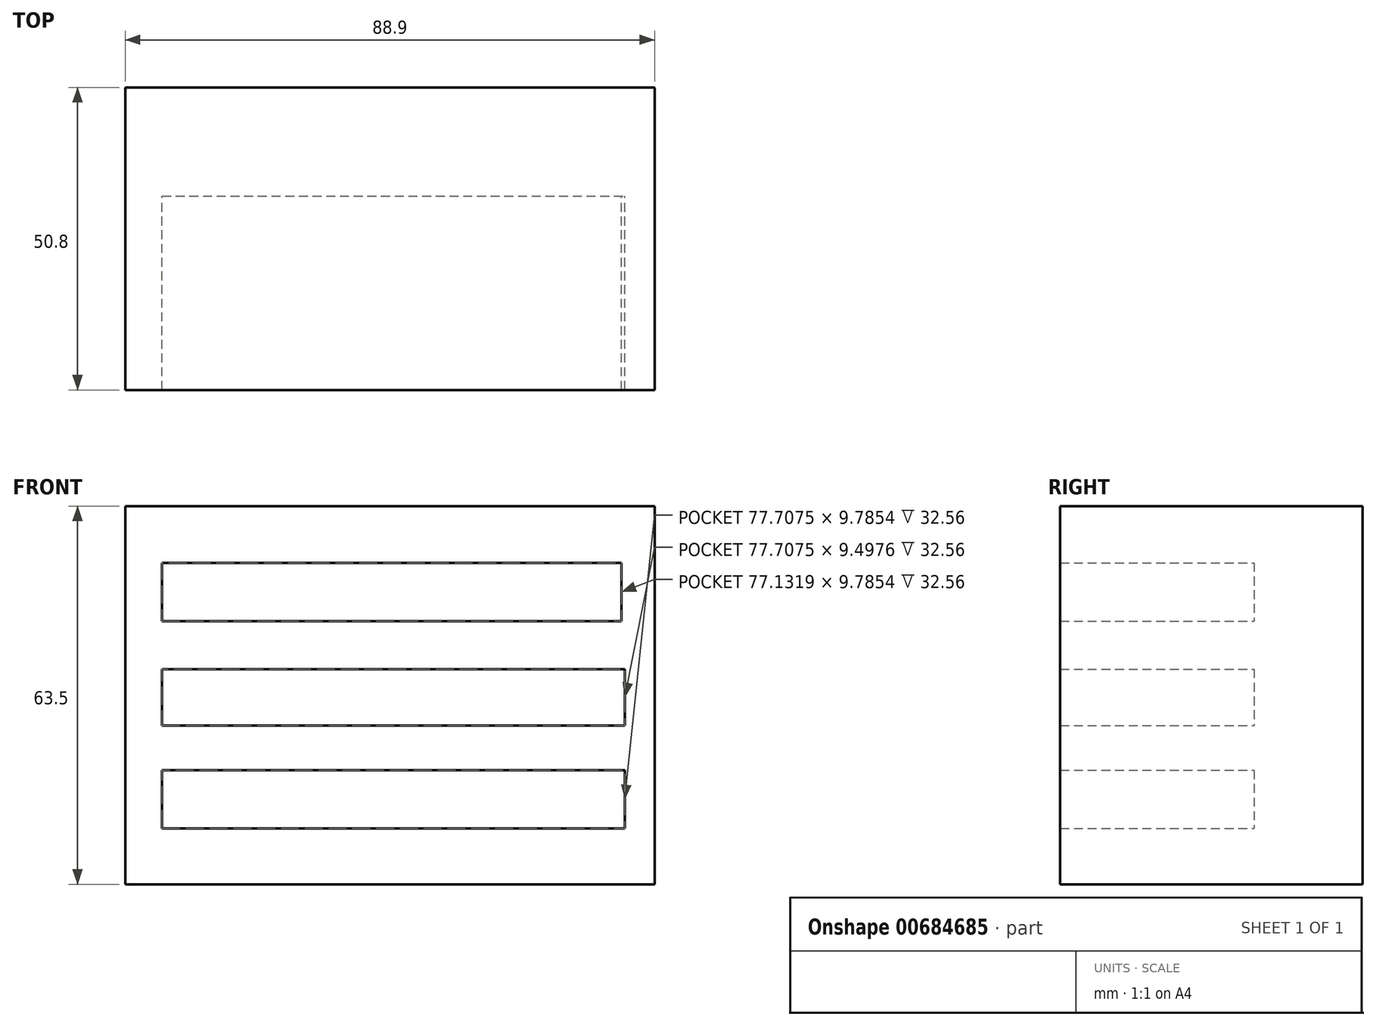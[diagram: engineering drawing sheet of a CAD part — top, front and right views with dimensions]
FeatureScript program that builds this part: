
annotation { "Feature Type Name" : "Feature", "Feature Type Description" : "" }
export const myFeature = defineFeature(function(context is Context, id is Id, definition is map)
    precondition{}
    {
        {
            var Q0;
            Q0=qCreatedBy(makeId("Top.planeOp"),FACE);
            var sketch = newSketch(context, id + "F0", { "sketchPlane" : qUnion([Q0])});
            skLineSegment(sketch, "E0.bottom", {"start": v(-37.69, 18.24) * mm, "end": v(51.21, 18.24) * mm});
            skLineSegment(sketch, "E0.top", {"start": v(-37.69, -32.56) * mm, "end": v(51.21, -32.56) * mm});
            skLineSegment(sketch, "E0.left", {"start": v(-37.69, 18.24) * mm, "end": v(-37.69, -32.56) * mm});
            skLineSegment(sketch, "E0.right", {"start": v(51.21, 18.24) * mm, "end": v(51.21, -32.56) * mm});
            skSolve(sketch);
        }
        {
            var Q0;
            Q0=qSketchRegion(id+"F0",true);
            extrude(context, id + "F1", {"entities" : qUnion([Q0]), "depth" : 63.5 * mm, "offsetDistance" : 25.4 * mm});
        }
        {
            var Q0;
            Q0=qCreatedBy(makeId("Front.planeOp"),FACE);
            var sketch = newSketch(context, id + "F2", { "sketchPlane" : qUnion([Q0])});
            skLineSegment(sketch, "E1.bottom", {"start": v(-31.51, 53.96) * mm, "end": v(45.62, 53.96) * mm});
            skLineSegment(sketch, "E1.top", {"start": v(-31.51, 44.18) * mm, "end": v(45.62, 44.18) * mm});
            skLineSegment(sketch, "E1.left", {"start": v(-31.51, 53.96) * mm, "end": v(-31.51, 44.18) * mm});
            skLineSegment(sketch, "E1.right", {"start": v(45.62, 53.96) * mm, "end": v(45.62, 44.18) * mm});
            skLineSegment(sketch, "E2.bottom", {"start": v(-31.51, 36.12) * mm, "end": v(46.2, 36.12) * mm});
            skLineSegment(sketch, "E2.top", {"start": v(-31.51, 26.62) * mm, "end": v(46.2, 26.62) * mm});
            skLineSegment(sketch, "E2.left", {"start": v(-31.51, 36.12) * mm, "end": v(-31.51, 26.62) * mm});
            skLineSegment(sketch, "E2.right", {"start": v(46.2, 36.12) * mm, "end": v(46.2, 26.62) * mm});
            skLineSegment(sketch, "E3.bottom", {"start": v(-31.51, 19.14) * mm, "end": v(46.2, 19.14) * mm});
            skLineSegment(sketch, "E3.top", {"start": v(-31.51, 9.35) * mm, "end": v(46.2, 9.35) * mm});
            skLineSegment(sketch, "E3.left", {"start": v(-31.51, 19.14) * mm, "end": v(-31.51, 9.35) * mm});
            skLineSegment(sketch, "E3.right", {"start": v(46.2, 19.14) * mm, "end": v(46.2, 9.35) * mm});
            skSolve(sketch);
        }
        {
            var Q0;
            Q0=qSketchRegion(id+"F2",true);
            extrude(context, id + "F3", {"entities" : qUnion([Q0]), "operationType" : NewBodyOperationType.REMOVE, "depth" : 127 * mm, "offsetDistance" : 25.4 * mm});
        }
    });
